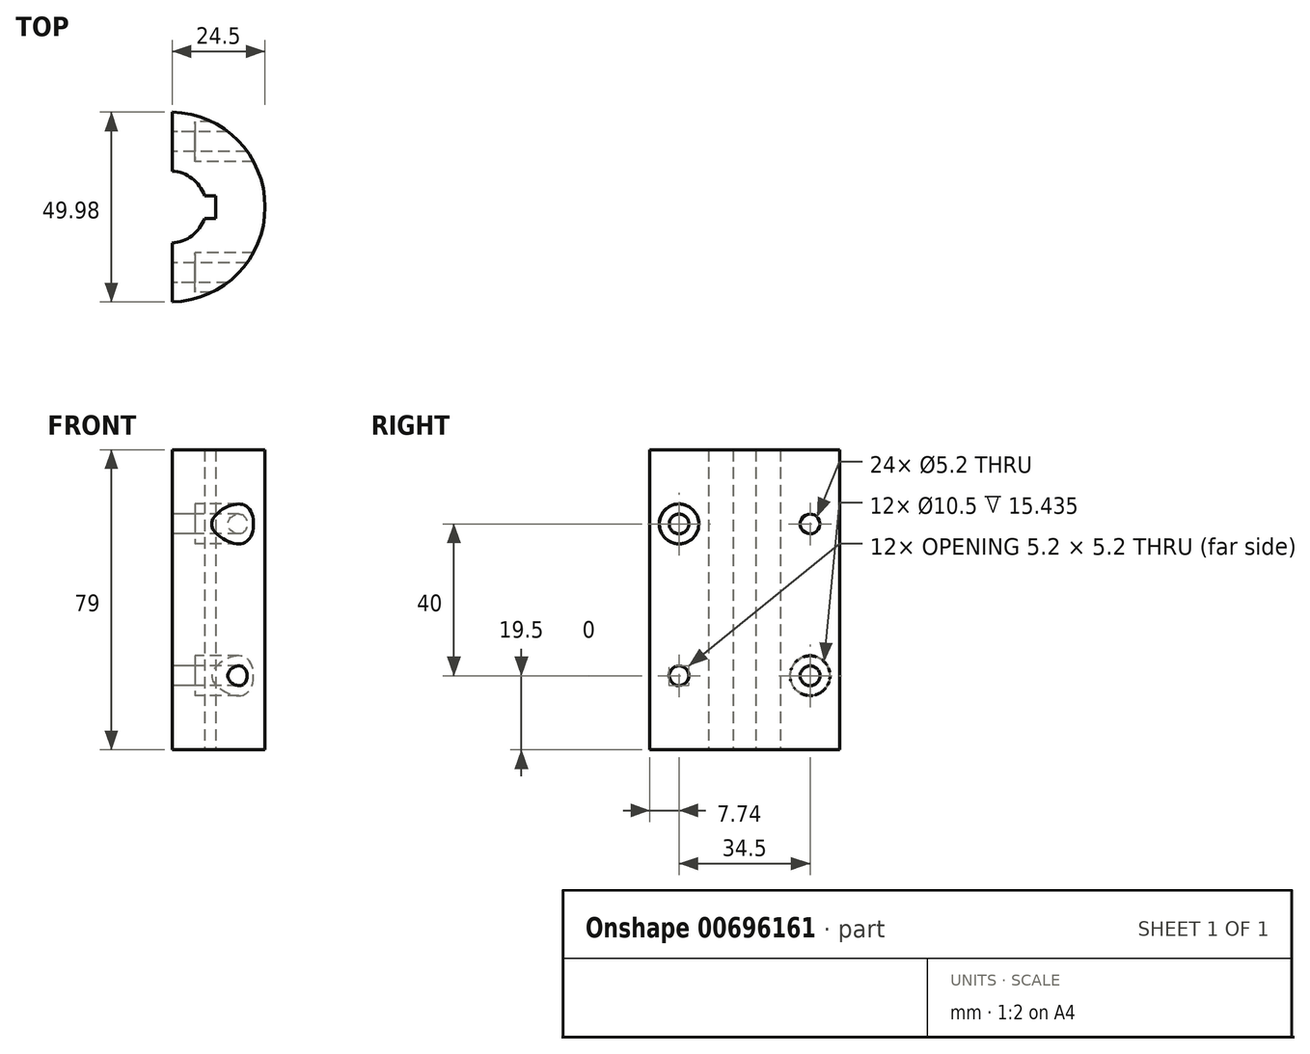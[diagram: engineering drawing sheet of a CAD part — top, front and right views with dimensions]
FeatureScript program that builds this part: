
annotation { "Feature Type Name" : "Feature", "Feature Type Description" : "" }
export const myFeature = defineFeature(function(context is Context, id is Id, definition is map)
    precondition{}
    {
        {
            var Q0;
            Q0=qCreatedBy(makeId("Top.planeOp"),FACE);
            var sketch = newSketch(context, id + "F0", { "sketchPlane" : qUnion([Q0])});
            skArc(sketch, "E0", {"start": v(0.5, -25) * mm, "mid": v(25, 0) * mm, "end": v(0.5, 25) * mm});
            skArc(sketch, "E1", {"start": v(0.5, -9.49) * mm, "mid": v(9.5, 0) * mm, "end": v(0.5, 9.49) * mm});
            skLineSegment(sketch, "E2", {"start": v(0.5, 25) * mm, "end": v(0.5, 9.49) * mm});
            skLineSegment(sketch, "E3", {"start": v(0.5, -9.49) * mm, "end": v(0.5, -25) * mm});
            skLineSegment(sketch, "E4", {"start": v(0, -30.05) * mm, "end": v(0, 31.88) * mm, "construction": true});
            skSolve(sketch);
        }
        {
            var Q0;
            Q0=qSketchRegion(id+"F0",true);
            extrude(context, id + "F1", {"entities" : qUnion([Q0]), "depth" : 79 * mm, "offsetDistance" : 25 * mm});
        }
        {
            var Q0;
            Q0=qCreatedBy(makeId("Right.planeOp"),FACE);
            var sketch = newSketch(context, id + "F2", { "sketchPlane" : qUnion([Q0])});
            skCircle(sketch, "E5", {"center": v(-17.25, 19.5) * mm, "radius": 2.6 * mm});
            skCircle(sketch, "E6", {"center": v(-17.25, 59.5) * mm, "radius": 2.6 * mm});
            skCircle(sketch, "E7", {"center": v(17.25, 59.5) * mm, "radius": 2.6 * mm});
            skCircle(sketch, "E8", {"center": v(17.25, 19.5) * mm, "radius": 2.6 * mm});
            skSolve(sketch);
        }
        {
            var Q0;
            Q0=qSketchRegion(id+"F2",true);
            extrude(context, id + "F3", {"entities" : qUnion([Q0]), "operationType" : NewBodyOperationType.REMOVE, "endBound" : BoundingType.THROUGH_ALL, "depth" : 25 * mm});
        }
        {
            var Q0;
            Q0=makeQuery(id+"F1.opExtrude","SWEPT_FACE",FACE,{"disambiguationData":[OSD([sQuery(id+"F0.wireOp",EDGE,"E3")])]});
            cPlane(context, id + "F4", {"entities" : qUnion([Q0]), "cplaneType" : CPlaneType.OFFSET, "offset" : 6 * mm, "oppositeDirection" : true, "width" : 150 * mm, "height" : 150 * mm});
        }
        {
            var Q0;
            Q0=qCreatedBy(id+"F4.planeOp",FACE);
            var sketch = newSketch(context, id + "F5", { "sketchPlane" : qUnion([Q0])});
            skCircle(sketch, "E9", {"center": v(17.25, 59.5) * mm, "radius": 5.25 * mm});
            skLineSegment(sketch, "E10", {"start": v(17.25, 59.5) * mm, "end": v(-17.25, 59.5) * mm});
            skCircle(sketch, "E11", {"center": v(-17.25, 19.5) * mm, "radius": 5.25 * mm});
            skLineSegment(sketch, "E12", {"start": v(-17.25, 59.5) * mm, "end": v(-17.25, 19.5) * mm});
            skSolve(sketch);
        }
        {
            var Q0;
            Q0=qSketchRegion(id+"F5",true);
            extrude(context, id + "F6", {"entities" : qUnion([Q0]), "operationType" : NewBodyOperationType.REMOVE, "oppositeDirection" : true, "depth" : 25 * mm});
        }
        {
            var Q0;
            Q0=qCreatedBy(makeId("Top.planeOp"),FACE);
            var sketch = newSketch(context, id + "F7", { "sketchPlane" : qUnion([Q0])});
            skLineSegment(sketch, "E13.bottom", {"start": v(12, 3) * mm, "end": v(6, 3) * mm});
            skLineSegment(sketch, "E13.top", {"start": v(12, -3) * mm, "end": v(6, -3) * mm});
            skLineSegment(sketch, "E13.left", {"start": v(12, 3) * mm, "end": v(12, -3) * mm});
            skLineSegment(sketch, "E13.right", {"start": v(6, 3) * mm, "end": v(6, -3) * mm});
            skPoint(sketch, "E13.middle", {"position": v(9, 0) * mm});
            skSolve(sketch);
        }
        {
            var Q0;
            Q0=qSketchRegion(id+"F7",true);
            extrude(context, id + "F8", {"entities" : qUnion([Q0]), "operationType" : NewBodyOperationType.REMOVE, "endBound" : BoundingType.THROUGH_ALL, "depth" : 25 * mm});
        }
    });
